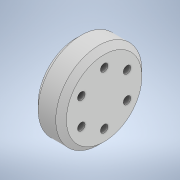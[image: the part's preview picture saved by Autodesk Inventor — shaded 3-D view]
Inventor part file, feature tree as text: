
AUTODESK INVENTOR PART (.ipt)
format: ipt  version: 2022 (Build 260153000, 153)  size: 178,688 bytes
history: native  units: mm
features: sketch x4, revolve x2, hole x2, other x1, thread x1
ambient origin geometry x8: Origin, YZ Plane, XZ Plane, XY Plane, X Axis, Y Axis, Z Axis, Center Point
bodies: Body1 (feature_tree)
feature tree (10):
  other  "Твердое тело1"
  revolve  "Вращение1"
  hole  "Отверстие1"  [1 undecoded]
  hole  "Отверстие2"  [1 undecoded]
  revolve  "Вращение2"
  thread  "Резьба1"
  sketch  "Эскиз1"
  sketch  "Эскиз2"
  sketch  "Эскиз3"
  sketch  "Эскиз4"
note: 2 required parameter values undecoded (feature->parameter linkage not recoverable at this tier; creation-order binding heuristic only, values carry confidence <= 0.55)
